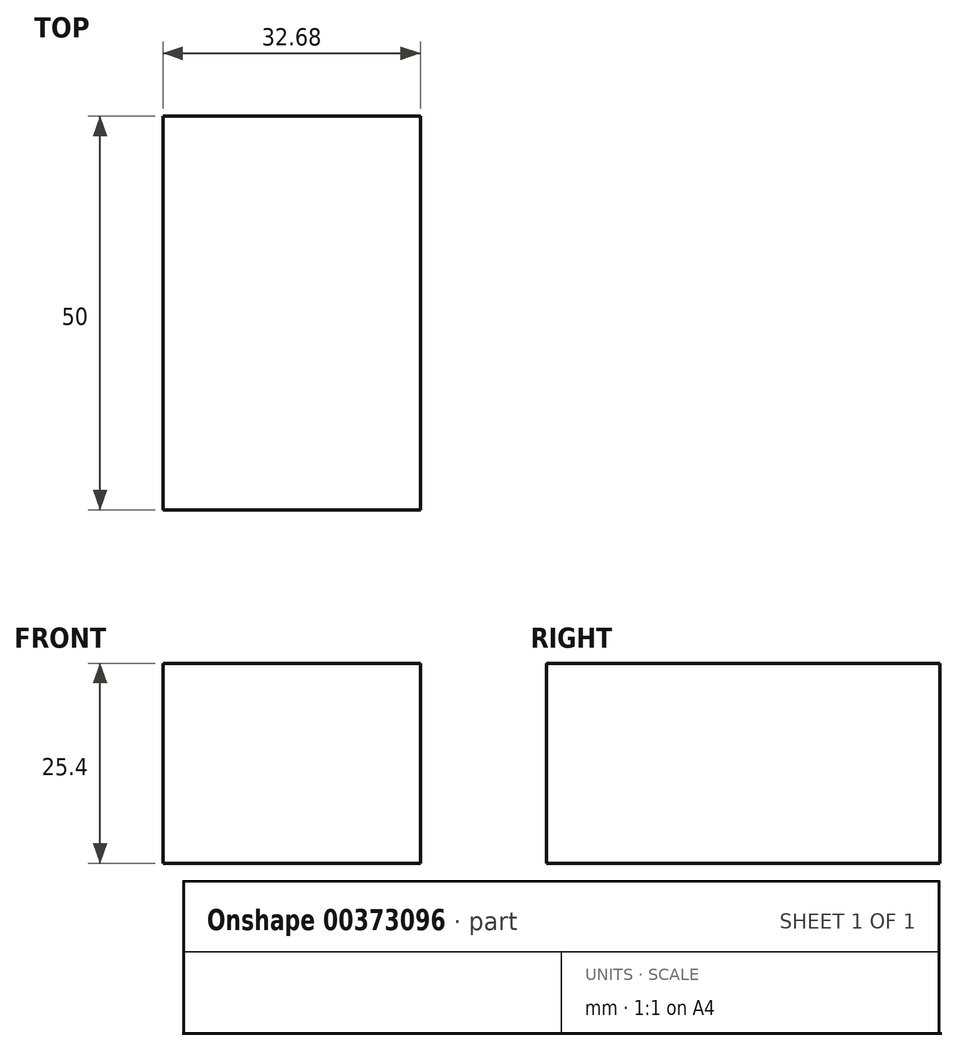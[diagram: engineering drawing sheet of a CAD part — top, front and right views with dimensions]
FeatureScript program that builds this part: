
annotation { "Feature Type Name" : "Feature", "Feature Type Description" : "" }
export const myFeature = defineFeature(function(context is Context, id is Id, definition is map)
    precondition{}
    {
        {
            var Q0;
            Q0=qCreatedBy(makeId("Top.planeOp"),FACE);
            var sketch = newSketch(context, id + "F0", { "sketchPlane" : qUnion([Q0])});
            skLineSegment(sketch, "E0.bottom", {"start": v(16.34, 25) * mm, "end": v(-16.34, 25) * mm});
            skLineSegment(sketch, "E0.top", {"start": v(16.34, -25) * mm, "end": v(-16.34, -25) * mm});
            skLineSegment(sketch, "E0.left", {"start": v(16.34, 25) * mm, "end": v(16.34, -25) * mm});
            skLineSegment(sketch, "E0.right", {"start": v(-16.34, 25) * mm, "end": v(-16.34, -25) * mm});
            skPoint(sketch, "E0.middle", {"position": v(0, 0) * mm});
            skSolve(sketch);
        }
        {
            var Q0;
            Q0=makeQuery(id+"F0.imprint","IMPRINT",FACE,{"disambiguationData":[TD([[makeQuery(id+"F0.imprint","IMPRINT",EDGE,{"derivedFrom":sQuery(id+"F0.wireOp",EDGE,"E0.bottom")}),1.0]])]});
            var Q1;
            Q1 = qSketchRegion(id + "F0", true);
            extrude(context, id + "F1", {"entities" : qUnion([Q0, Q1]), "depth" : 25.4 * mm});
        }
    });
